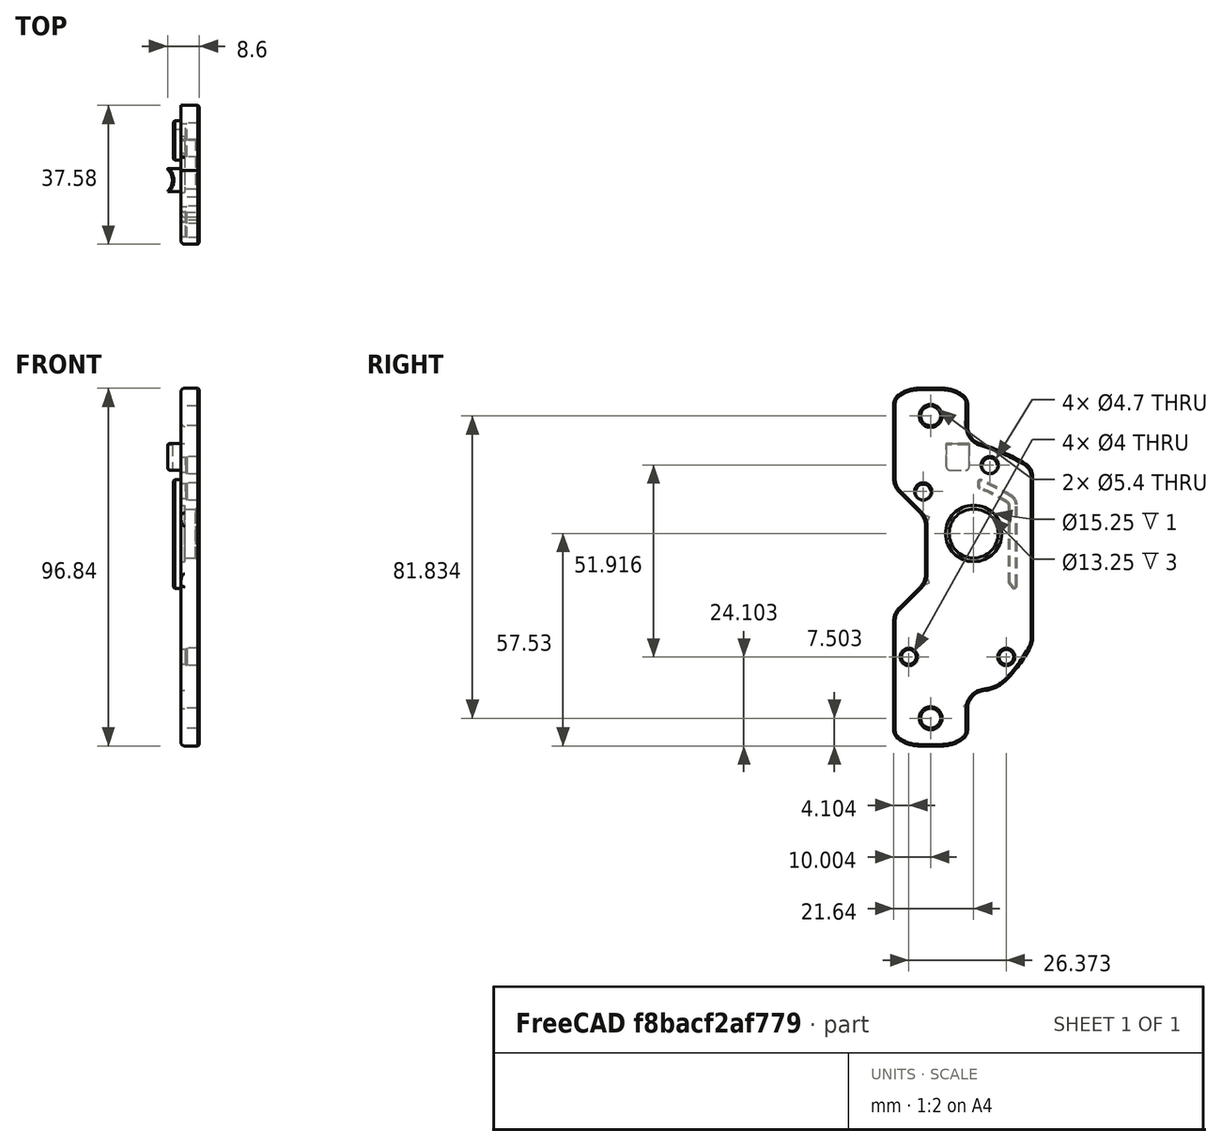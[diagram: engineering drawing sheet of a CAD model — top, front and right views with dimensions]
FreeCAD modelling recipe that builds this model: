
FCSTD DOCUMENT  (FreeCAD 0.21R33771 (Git))
Label: 9
License: All rights reserved
LicenseURL: http://en.wikipedia.org/wiki/All_rights_reserved
objects: Part::Feature×1, PartDesign::FeatureBase×1, Sketcher::SketchObject×1, PartDesign::Pocket×1, PartDesign::Body×1
note: 6 computed .brp shape members not serialized (recipe doc carries the construction recipe); baked Part::Feature solids carry a one-line shape summary decoded from their .brp

FEATURE [Part::Feature] Part__Feature020  label="End Plate"
  shape: bbox 10.02 x 38 x 98.42 mm, 140 faces (baked)
FEATURE [PartDesign::FeatureBase] BaseFeature
  BaseFeature = -> Part__Feature020
FEATURE [Sketcher::SketchObject] Sketch
  ExternalGeometry = -> [BaseFeature]
  FullyConstrained = true
  MapMode = 5
  Placement = pos=(-3.5,0,2e-16) rot=(0.57735,-0.57735,-0.57735;2.0944rad)
  Support = -> [BaseFeature]
  sketch-geometry (4):
    g0: Circle CenterX=13.65 CenterY=11.3596 CenterZ=0 NormalX=0 NormalY=0 NormalZ=1 AngleXU=0 Radius=2
    g1: Circle CenterX=-4.35 CenterY=18.4894 CenterZ=0 NormalX=0 NormalY=0 NormalZ=1 AngleXU=0 Radius=2
    g2: Circle CenterX=17.5364 CenterY=-33.427 CenterZ=0 NormalX=0 NormalY=0 NormalZ=1 AngleXU=0 Radius=2
    g3: Circle CenterX=-8.83642 CenterY=-33.427 CenterZ=0 NormalX=0 NormalY=0 NormalZ=1 AngleXU=0 Radius=2
  constraints (8):
    c: Coincident(g0,g-3)
    c: Coincident(g1,g-4)
    c: Coincident(g2,g-5)
    c: Coincident(g3,g-6)
    c: Equal(g2,g3)
    c: Equal(g3,g0)
    c: Equal(g0,g1)
    c: Diameter(g0) = 4
FEATURE [PartDesign::Pocket] Pocket
  BaseFeature = -> BaseFeature
  Direction = (1,0,0)
  Length = 5
  Length2 = 5
  Profile = -> Sketch
  ReferenceAxis = -> Sketch [N_Axis]
  Type = 1
FEATURE [PartDesign::Body] Body
  BaseFeature = -> Part__Feature020
  Group = -> [BaseFeature,Sketch,Pocket]
  Origin = -> Origin
  Tip = -> Pocket
